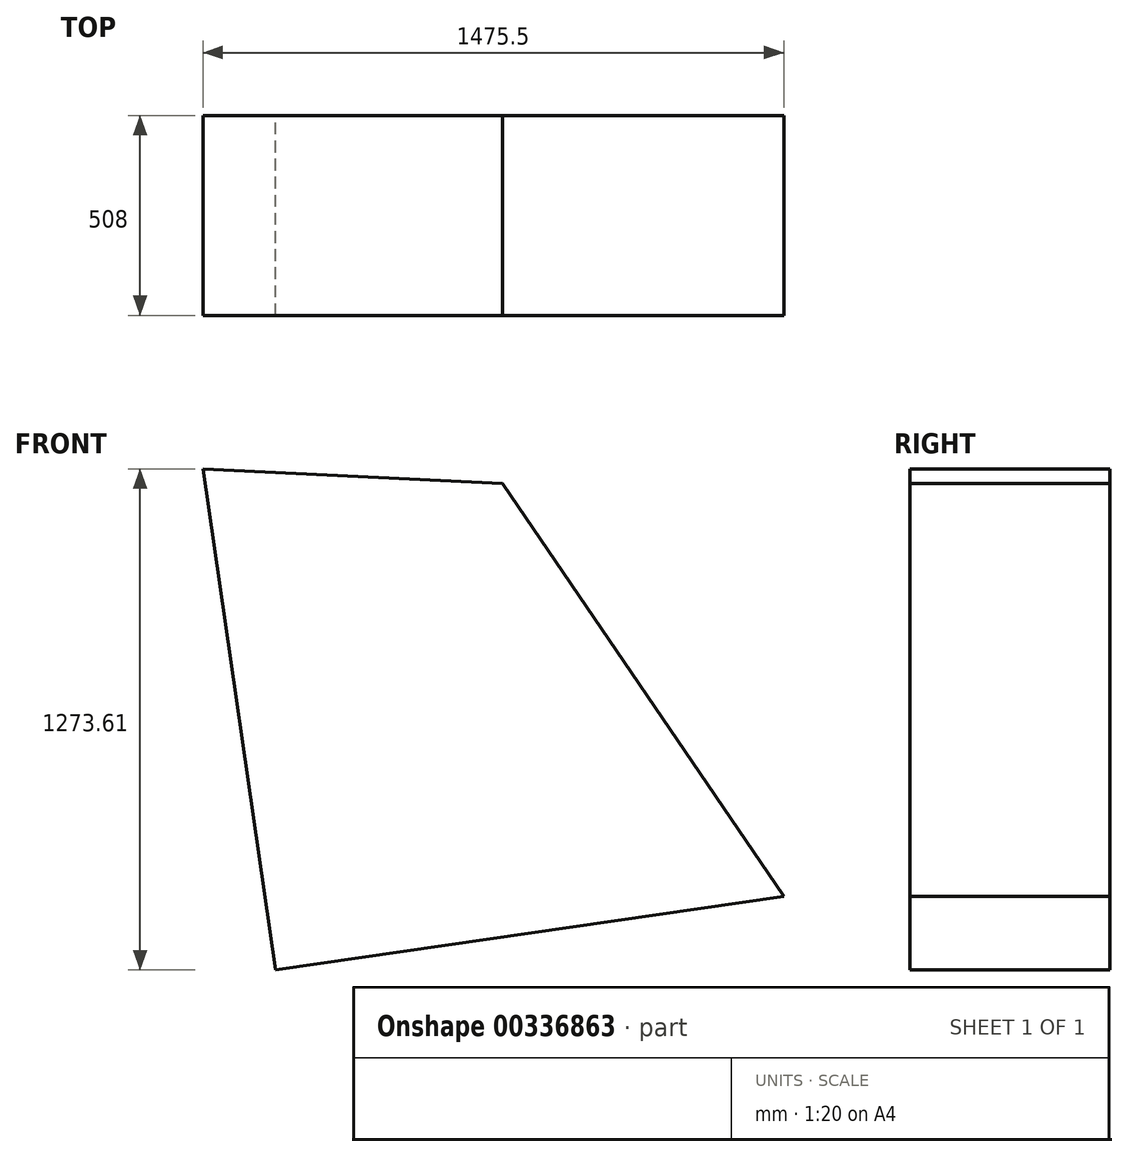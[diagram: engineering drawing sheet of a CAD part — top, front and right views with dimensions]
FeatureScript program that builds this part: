
annotation { "Feature Type Name" : "Feature", "Feature Type Description" : "" }
export const myFeature = defineFeature(function(context is Context, id is Id, definition is map)
    precondition{}
    {
        {
            var Q0;
            Q0=qCreatedBy(makeId("Front.planeOp"),FACE);
            var sketch = newSketch(context, id + "F0", { "sketchPlane" : qUnion([Q0])});
            skLineSegment(sketch, "E0", {"start": v(-559.2, -640.36) * mm, "end": v(732.09, -453.6) * mm});
            skLineSegment(sketch, "E1", {"start": v(732.09, -453.6) * mm, "end": v(17.7, 596.42) * mm});
            skLineSegment(sketch, "E2", {"start": v(17.7, 596.42) * mm, "end": v(-743.41, 633.25) * mm});
            skLineSegment(sketch, "E3", {"start": v(-743.41, 633.25) * mm, "end": v(-559.2, -640.36) * mm});
            skSolve(sketch);
        }
        {
            var Q0;
            Q0 = qSketchRegion(id + "F0", true);
            extrude(context, id + "F1", {"entities" : qUnion([Q0]), "depth" : 508 * mm});
        }
    });
